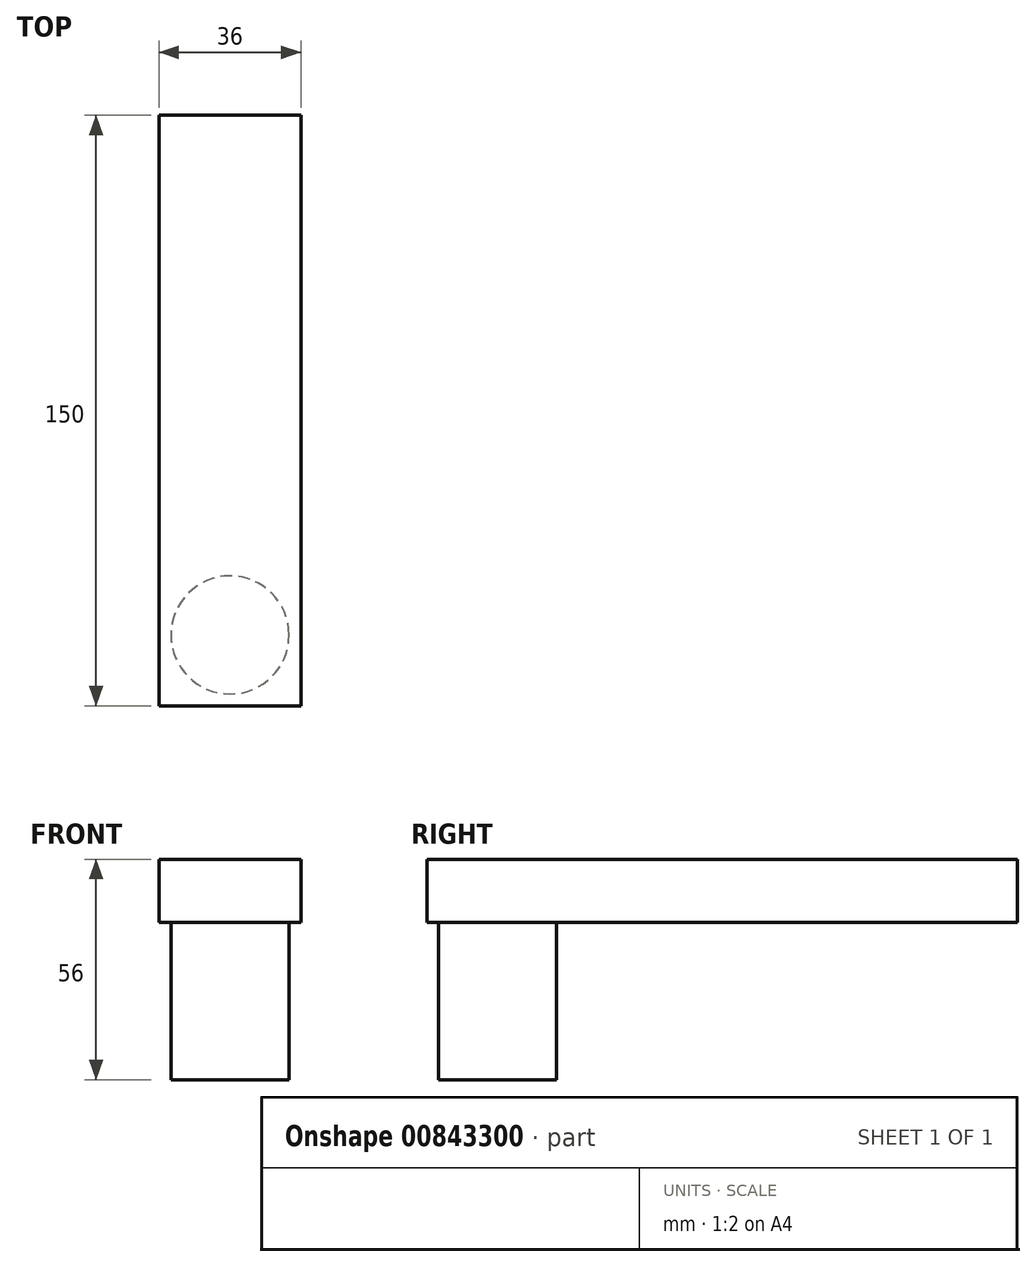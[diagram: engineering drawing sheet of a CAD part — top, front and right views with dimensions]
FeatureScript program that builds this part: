
annotation { "Feature Type Name" : "Feature", "Feature Type Description" : "" }
export const myFeature = defineFeature(function(context is Context, id is Id, definition is map)
    precondition{}
    {
        {
            var Q0;
            Q0=qCreatedBy(makeId("Front.planeOp"),FACE);
            var sketch = newSketch(context, id + "F0", { "sketchPlane" : qUnion([Q0])});
            skLineSegment(sketch, "E0.bottom", {"start": v(-5.76, -11.1) * mm, "end": v(30.24, -11.1) * mm});
            skLineSegment(sketch, "E0.top", {"start": v(-5.76, -27.1) * mm, "end": v(30.24, -27.1) * mm});
            skLineSegment(sketch, "E0.left", {"start": v(-5.76, -11.1) * mm, "end": v(-5.76, -27.1) * mm});
            skLineSegment(sketch, "E0.right", {"start": v(30.24, -11.1) * mm, "end": v(30.24, -27.1) * mm});
            skSolve(sketch);
        }
        {
            var Q0;
            Q0 = qSketchRegion(id + "F0", true);
            extrude(context, id + "F1", {"entities" : qUnion([Q0]), "depth" : 150 * mm, "offsetDistance" : 25 * mm});
        }
        {
            var Q0;
            Q0=makeQuery(id+"F1.opExtrude","SWEPT_FACE",FACE,{"disambiguationData":[OSD([sQuery(id+"F0.wireOp",EDGE,"E0.top")])]});
            var sketch = newSketch(context, id + "F2", { "sketchPlane" : qUnion([Q0])});
            skCircle(sketch, "E1", {"center": v(12.24, 132) * mm, "radius": 15 * mm});
            skSolve(sketch);
        }
        {
            var Q0;
            Q0=makeQuery(id+"F2.imprint","IMPRINT",FACE,{"disambiguationData":[TD([[makeQuery(id+"F2.imprint","IMPRINT",EDGE,{"derivedFrom":sQuery(id+"F2.wireOp",EDGE,"E1")}),1.0]])]});
            var Q1;
            Q1=sQuery(id+"F2.wireOp",EDGE,"E1");
            extrude(context, id + "F3", {"entities" : qUnion([Q0]), "operationType" : NewBodyOperationType.ADD, "surfaceEntities" : qUnion([Q1]), "depth" : 40 * mm, "offsetDistance" : 25 * mm});
        }
    });
